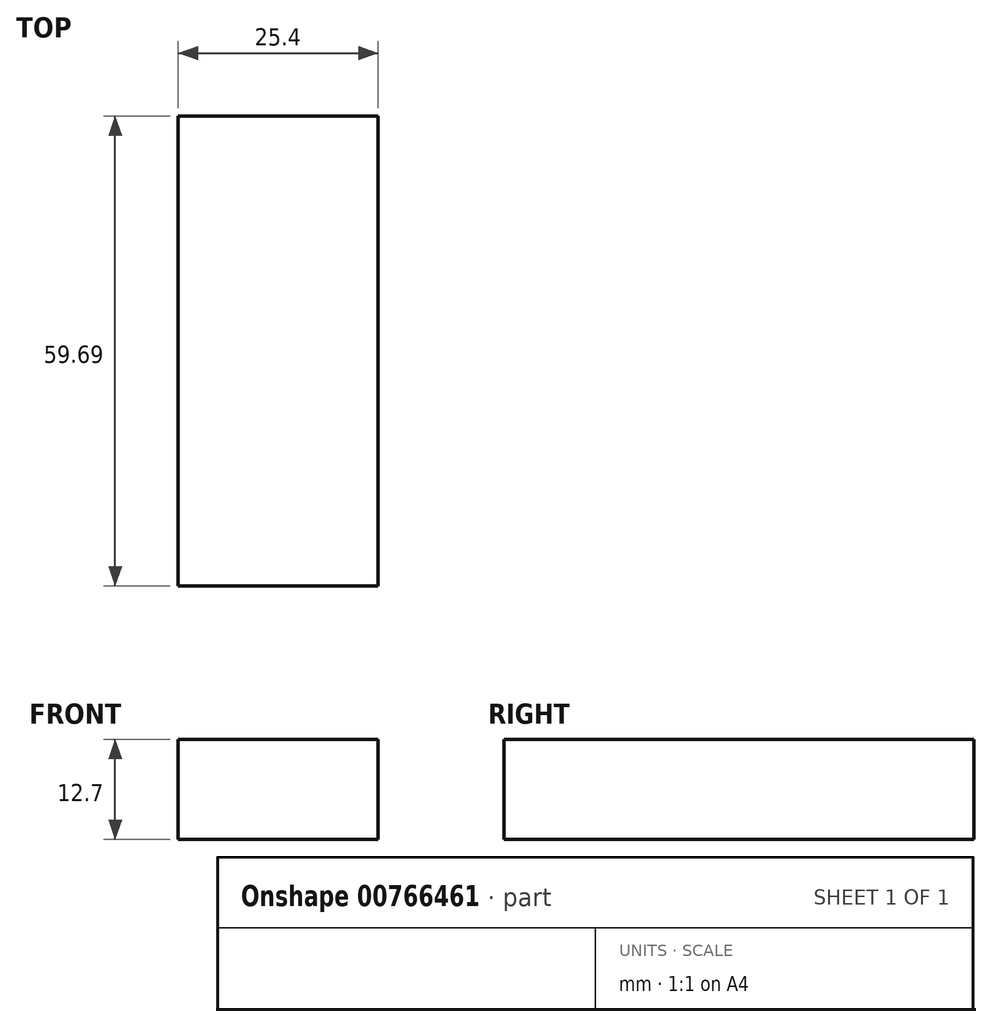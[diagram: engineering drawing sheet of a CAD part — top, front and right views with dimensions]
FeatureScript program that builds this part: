
annotation { "Feature Type Name" : "Feature", "Feature Type Description" : "" }
export const myFeature = defineFeature(function(context is Context, id is Id, definition is map)
    precondition{}
    {
        {
            var Q0;
            Q0=qCreatedBy(makeId("Front.planeOp"),FACE);
            var sketch = newSketch(context, id + "F0", { "sketchPlane" : qUnion([Q0])});
            skLineSegment(sketch, "E0.bottom", {"start": v(-25.4, 0) * mm, "end": v(0, 0) * mm});
            skLineSegment(sketch, "E0.top", {"start": v(-25.4, 12.7) * mm, "end": v(0, 12.7) * mm});
            skLineSegment(sketch, "E0.left", {"start": v(-25.4, 0) * mm, "end": v(-25.4, 12.7) * mm});
            skLineSegment(sketch, "E0.right", {"start": v(0, 0) * mm, "end": v(0, 12.7) * mm});
            skSolve(sketch);
        }
        {
            var Q0;
            Q0=makeQuery(id+"F0.imprint","IMPRINT",FACE,{"disambiguationData":[TD([[makeQuery(id+"F0.imprint","IMPRINT",EDGE,{"derivedFrom":sQuery(id+"F0.wireOp",EDGE,"E0.bottom")}),1.0]])]});
            extrude(context, id + "F1", {"entities" : qUnion([Q0]), "depth" : 59.69 * mm, "offsetDistance" : 25.4 * mm});
        }
    });
